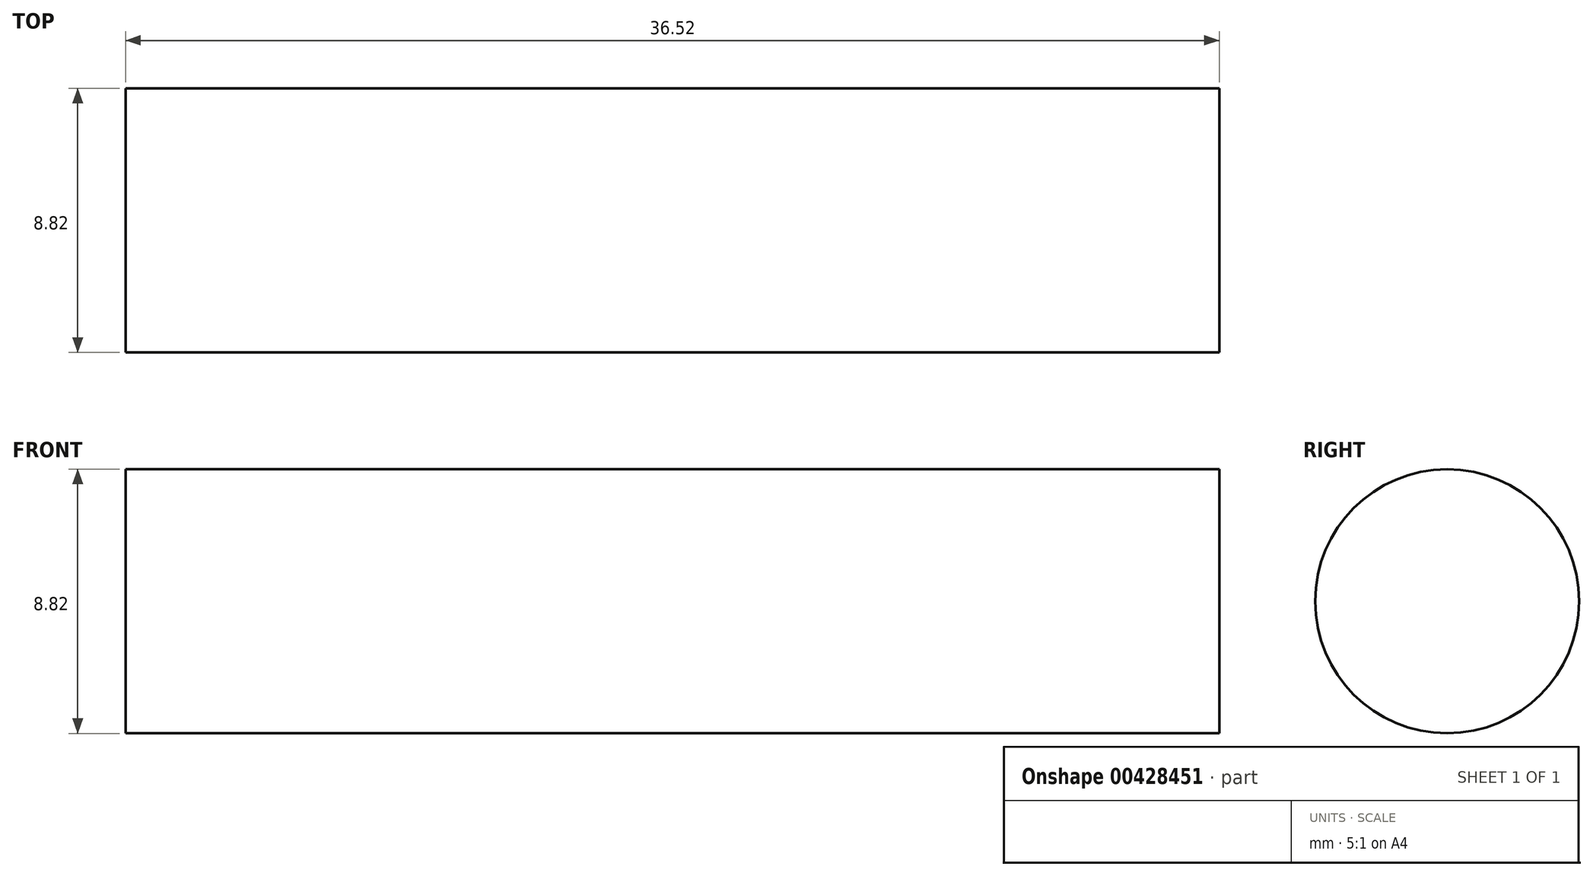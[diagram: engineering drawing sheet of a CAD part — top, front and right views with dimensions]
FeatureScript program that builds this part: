
annotation { "Feature Type Name" : "Feature", "Feature Type Description" : "" }
export const myFeature = defineFeature(function(context is Context, id is Id, definition is map)
    precondition{}
    {
        {
            var Q0;
            Q0=qCreatedBy(makeId("Right.planeOp"),FACE);
            var sketch = newSketch(context, id + "F0", { "sketchPlane" : qUnion([Q0])});
            skCircle(sketch, "E0", {"center": v(0, 0) * mm, "radius": 4.4 * mm});
            skSolve(sketch);
        }
        {
            var Q0;
            Q0=makeQuery(id+"F0.imprint","IMPRINT",FACE,{"disambiguationData":[TD([[makeQuery(id+"F0.imprint","IMPRINT",EDGE,{"derivedFrom":sQuery(id+"F0.wireOp",EDGE,"E0")}),1.0]])]});
            extrude(context, id + "F1", {"entities" : qUnion([Q0]), "depth" : 18.26 * mm, "hasSecondDirection" : true, "secondDirectionOppositeDirection" : true, "secondDirectionDepth" : 18.26 * mm});
        }
    });
